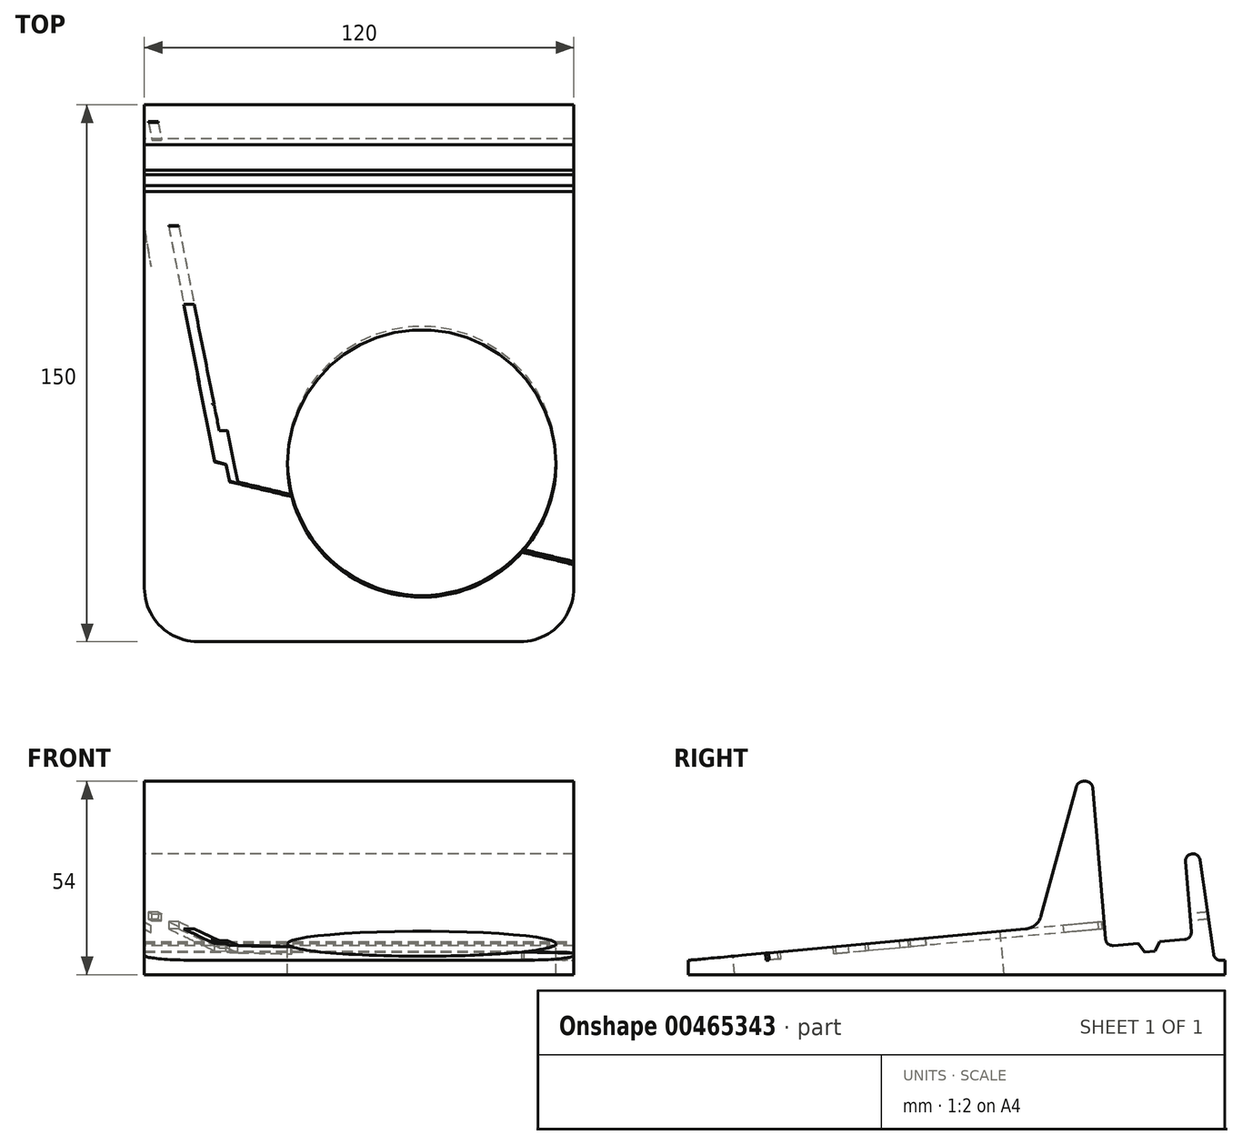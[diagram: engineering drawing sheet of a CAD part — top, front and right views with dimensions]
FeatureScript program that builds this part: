
annotation { "Feature Type Name" : "Feature", "Feature Type Description" : "" }
export const myFeature = defineFeature(function(context is Context, id is Id, definition is map)
    precondition{}
    {
        {
            var Q0;
            Q0=qCreatedBy(makeId("Right.planeOp"),FACE);
            var sketch = newSketch(context, id + "F0", { "sketchPlane" : qUnion([Q0])});
            skLineSegment(sketch, "E0", {"start": v(0, 0) * mm, "end": v(0, 4) * mm});
            skLineSegment(sketch, "E1", {"start": v(150, 4) * mm, "end": v(150, 0) * mm});
            skLineSegment(sketch, "E2", {"start": v(150, 0) * mm, "end": v(0, 0) * mm});
            skLineSegment(sketch, "E3", {"start": v(150, 4) * mm, "end": v(148.73, 4) * mm});
            skLineSegment(sketch, "E4", {"start": v(146.75, 5.71) * mm, "end": v(142.68, 34) * mm});
            skLineSegment(sketch, "E5", {"start": v(142.68, 34) * mm, "end": v(138.72, 33.43) * mm});
            skLineSegment(sketch, "E6", {"start": v(138.72, 33.43) * mm, "end": v(140.53, 12) * mm});
            skPoint(sketch, "E6.endSnap0", {"position": v(140.7, 33.71) * mm});
            skLineSegment(sketch, "E7", {"start": v(138.7, 9.83) * mm, "end": v(118.7, 8.14) * mm});
            skLineSegment(sketch, "E8", {"start": v(116.54, 9.97) * mm, "end": v(112.82, 54) * mm});
            skLineSegment(sketch, "E9", {"start": v(112.82, 54) * mm, "end": v(108.82, 54) * mm});
            skLineSegment(sketch, "E10", {"start": v(108.82, 54) * mm, "end": v(98.58, 16.42) * mm});
            skLineSegment(sketch, "E11", {"start": v(94.22, 12.76) * mm, "end": v(0, 4) * mm});
            skPoint(sketch, "E12.visualSharp", {"position": v(147, 4) * mm});
            skArc(sketch, "E12.filletArc", {"start": v(146.75, 5.71) * mm, "mid": v(147.42, 4.49) * mm, "end": v(148.73, 4) * mm});
            skPoint(sketch, "E13.visualSharp", {"position": v(97.67, 13.08) * mm});
            skArc(sketch, "E13.filletArc", {"start": v(94.22, 12.76) * mm, "mid": v(96.97, 13.91) * mm, "end": v(98.58, 16.42) * mm});
            skPoint(sketch, "E14.visualSharp", {"position": v(116.71, 7.97) * mm});
            skArc(sketch, "E14.filletArc", {"start": v(116.54, 9.97) * mm, "mid": v(117.25, 8.6) * mm, "end": v(118.7, 8.14) * mm});
            skPoint(sketch, "E15.visualSharp", {"position": v(140.7, 10) * mm});
            skArc(sketch, "E15.filletArc", {"start": v(138.7, 9.83) * mm, "mid": v(140.06, 10.53) * mm, "end": v(140.53, 12) * mm});
            skSolve(sketch);
        }
        {
            var Q0;
            Q0=qSketchRegion(id+"F0",true);
            extrude(context, id + "F1", {"entities" : qUnion([Q0]), "offsetDistance" : 25 * mm, "depth" : 120 * mm});
        }
        {
            var Q0;
            Q0=makeQuery(id+"F1.opExtrude","CAP_EDGE",EDGE,{"disambiguationData":[OSD([sQuery(id+"F0.wireOp",EDGE,"E0")])],"isStart":false});
            var Q1;
            Q1=makeQuery(id+"F1.opExtrude","CAP_EDGE",EDGE,{"disambiguationData":[OSD([sQuery(id+"F0.wireOp",EDGE,"E0")])],"isStart":true});
            fillet(context, id + "F2", {"entities" : qUnion([Q0, Q1]), "radius" : 15 * mm, "tangentPropagation" : true, "allowEdgeOverflow" : false});
        }
        {
            var Q0;
            Q0=makeQuery(id+"F1.opExtrude","SWEPT_EDGE",EDGE,{"disambiguationData":[OSD([sQuery(id+"F0.wireOp",EDGE,"E9"),sQuery(id+"F0.wireOp",EDGE,"E10")])]});
            var Q1;
            Q1=makeQuery(id+"F1.opExtrude","SWEPT_EDGE",EDGE,{"disambiguationData":[OSD([sQuery(id+"F0.wireOp",EDGE,"E8"),sQuery(id+"F0.wireOp",EDGE,"E9")])]});
            var Q2;
            Q2=makeQuery(id+"F1.opExtrude","SWEPT_EDGE",EDGE,{"disambiguationData":[OSD([sQuery(id+"F0.wireOp",EDGE,"E5"),sQuery(id+"F0.wireOp",EDGE,"E6")])]});
            var Q3;
            Q3=makeQuery(id+"F1.opExtrude","SWEPT_EDGE",EDGE,{"disambiguationData":[OSD([sQuery(id+"F0.wireOp",EDGE,"E4"),sQuery(id+"F0.wireOp",EDGE,"E5")])]});
            fillet(context, id + "F3", {"entities" : qUnion([Q0, Q1, Q2, Q3]), "radius" : 2 * mm, "tangentPropagation" : true, "allowEdgeOverflow" : false});
        }
        {
            var Q0;
            Q0=makeQuery(id+"F1.opExtrude","SWEPT_BODY",BODY,{"disambiguationData":[OSD([sQuery(id+"F0.wireOp",EDGE,"E0"),sQuery(id+"F0.wireOp",EDGE,"E1"),sQuery(id+"F0.wireOp",EDGE,"E2"),sQuery(id+"F0.wireOp",EDGE,"E3"),sQuery(id+"F0.wireOp",EDGE,"E4"),sQuery(id+"F0.wireOp",EDGE,"E5"),sQuery(id+"F0.wireOp",EDGE,"E6"),sQuery(id+"F0.wireOp",EDGE,"E7"),sQuery(id+"F0.wireOp",EDGE,"E8"),sQuery(id+"F0.wireOp",EDGE,"E9"),sQuery(id+"F0.wireOp",EDGE,"E10"),sQuery(id+"F0.wireOp",EDGE,"E11"),sQuery(id+"F0.wireOp",EDGE,"E12.filletArc"),sQuery(id+"F0.wireOp",EDGE,"E13.filletArc"),sQuery(id+"F0.wireOp",EDGE,"E14.filletArc"),sQuery(id+"F0.wireOp",EDGE,"E15.filletArc")])]});
            transform(context, id + "F4", {"entities" : qUnion([Q0]), "transformType" : TransformType.TRANSLATION_3D, "dx" : 0 * mm, "dy" : 0 * mm, "dz" : 0 * mm, "makeCopy" : true});
        }
        {
            var Q0;
            Q0=makeQuery(id+"F4.opPattern","COPY",FACE,{"derivedFrom":makeQuery(id+"F1.opExtrude","SWEPT_FACE",FACE,{"disambiguationData":[OSD([sQuery(id+"F0.wireOp",EDGE,"E11")])]}),"instanceName":"1"});
            var sketch = newSketch(context, id + "F5", { "sketchPlane" : qUnion([Q0])});
            skCircle(sketch, "E16", {"center": v(77.5, 50.37) * mm, "radius": 37.5 * mm});
            skSolve(sketch);
        }
        {
            var Q0;
            Q0=qSketchRegion(id+"F5",true);
            extrude(context, id + "F6", {"entities" : qUnion([Q0]), "operationType" : NewBodyOperationType.REMOVE, "oppositeDirection" : true, "depth" : 25 * mm});
        }
        {
            var Q0;
            Q0=makeQuery(id+"F1.opExtrude","SWEPT_BODY",BODY,{"disambiguationData":[OSD([sQuery(id+"F0.wireOp",EDGE,"E0"),sQuery(id+"F0.wireOp",EDGE,"E1"),sQuery(id+"F0.wireOp",EDGE,"E2"),sQuery(id+"F0.wireOp",EDGE,"E3"),sQuery(id+"F0.wireOp",EDGE,"E4"),sQuery(id+"F0.wireOp",EDGE,"E5"),sQuery(id+"F0.wireOp",EDGE,"E6"),sQuery(id+"F0.wireOp",EDGE,"E7"),sQuery(id+"F0.wireOp",EDGE,"E8"),sQuery(id+"F0.wireOp",EDGE,"E9"),sQuery(id+"F0.wireOp",EDGE,"E10"),sQuery(id+"F0.wireOp",EDGE,"E11"),sQuery(id+"F0.wireOp",EDGE,"E12.filletArc"),sQuery(id+"F0.wireOp",EDGE,"E13.filletArc"),sQuery(id+"F0.wireOp",EDGE,"E14.filletArc"),sQuery(id+"F0.wireOp",EDGE,"E15.filletArc")])]});
            transform(context, id + "F7", {"entities" : qUnion([Q0]), "transformType" : TransformType.TRANSLATION_3D, "dx" : 0 * mm, "dy" : 0 * mm, "dz" : 0 * mm, "makeCopy" : true});
        }
        {
            var Q0;
            Q0=makeQuery(id+"F1.opExtrude","SWEPT_BODY",BODY,{"disambiguationData":[OSD([sQuery(id+"F0.wireOp",EDGE,"E0"),sQuery(id+"F0.wireOp",EDGE,"E1"),sQuery(id+"F0.wireOp",EDGE,"E2"),sQuery(id+"F0.wireOp",EDGE,"E3"),sQuery(id+"F0.wireOp",EDGE,"E4"),sQuery(id+"F0.wireOp",EDGE,"E5"),sQuery(id+"F0.wireOp",EDGE,"E6"),sQuery(id+"F0.wireOp",EDGE,"E7"),sQuery(id+"F0.wireOp",EDGE,"E8"),sQuery(id+"F0.wireOp",EDGE,"E9"),sQuery(id+"F0.wireOp",EDGE,"E10"),sQuery(id+"F0.wireOp",EDGE,"E11"),sQuery(id+"F0.wireOp",EDGE,"E12.filletArc"),sQuery(id+"F0.wireOp",EDGE,"E13.filletArc"),sQuery(id+"F0.wireOp",EDGE,"E14.filletArc"),sQuery(id+"F0.wireOp",EDGE,"E15.filletArc")])]});
            deleteBodies(context, id + "F8", {"entities" : qUnion([Q0])});
        }
        {
            var Q0;
            Q0=makeQuery(id+"F4.opPattern","COPY",BODY,{"derivedFrom":makeQuery(id+"F1.opExtrude","SWEPT_BODY",BODY,{"disambiguationData":[OSD([sQuery(id+"F0.wireOp",EDGE,"E0"),sQuery(id+"F0.wireOp",EDGE,"E1"),sQuery(id+"F0.wireOp",EDGE,"E2"),sQuery(id+"F0.wireOp",EDGE,"E3"),sQuery(id+"F0.wireOp",EDGE,"E4"),sQuery(id+"F0.wireOp",EDGE,"E5"),sQuery(id+"F0.wireOp",EDGE,"E6"),sQuery(id+"F0.wireOp",EDGE,"E7"),sQuery(id+"F0.wireOp",EDGE,"E8"),sQuery(id+"F0.wireOp",EDGE,"E9"),sQuery(id+"F0.wireOp",EDGE,"E10"),sQuery(id+"F0.wireOp",EDGE,"E11"),sQuery(id+"F0.wireOp",EDGE,"E12.filletArc"),sQuery(id+"F0.wireOp",EDGE,"E13.filletArc"),sQuery(id+"F0.wireOp",EDGE,"E14.filletArc"),sQuery(id+"F0.wireOp",EDGE,"E15.filletArc")])]}),"instanceName":"1"});
            deleteBodies(context, id + "F9", {"entities" : qUnion([Q0])});
        }
        {
            var Q0;
            Q0=makeQuery(id+"F7.opPattern","COPY",FACE,{"derivedFrom":makeQuery(id+"F1.opExtrude","SWEPT_FACE",FACE,{"disambiguationData":[OSD([sQuery(id+"F0.wireOp",EDGE,"E11")])]}),"instanceName":"1"});
            var sketch = newSketch(context, id + "F10", { "sketchPlane" : qUnion([Q0])});
            skLineSegment(sketch, "E17", {"start": v(11.27, 59.35) * mm, "end": v(12.93, 59.25) * mm});
            skLineSegment(sketch, "E18", {"start": v(12.93, 59.25) * mm, "end": v(12.93, 52.54) * mm});
            skLineSegment(sketch, "E19", {"start": v(20.34, 67.04) * mm, "end": v(18.96, 67.04) * mm});
            skLineSegment(sketch, "E20", {"start": v(20.34, 62.07) * mm, "end": v(20.34, 64.54) * mm});
            skLineSegment(sketch, "E21", {"start": v(20.34, 64.54) * mm, "end": v(20.34, 67.04) * mm});
            skLineSegment(sketch, "E22", {"start": v(48.14, 58.86) * mm, "end": v(49.44, 58.75) * mm});
            skLineSegment(sketch, "E23", {"start": v(55.97, 56.74) * mm, "end": v(57.27, 57.87) * mm});
            skLineSegment(sketch, "E24", {"start": v(55.97, 50.67) * mm, "end": v(55.97, 56.74) * mm});
            skLineSegment(sketch, "E25", {"start": v(49.44, 58.75) * mm, "end": v(49.44, 52.05) * mm});
            skLineSegment(sketch, "E26", {"start": v(64.44, 56.14) * mm, "end": v(64.44, 50.74) * mm});
            skLineSegment(sketch, "E27", {"start": v(26.69, 60.97) * mm, "end": v(26.69, 62.28) * mm});
            skLineSegment(sketch, "E28", {"start": v(20.34, 53.81) * mm, "end": v(20.34, 59.63) * mm});
            skLineSegment(sketch, "E29", {"start": v(63.2, 57.41) * mm, "end": v(64.44, 56.14) * mm});
            skLineSegment(sketch, "E30", {"start": v(26.69, 59.63) * mm, "end": v(26.69, 60.97) * mm});
            skLineSegment(sketch, "E31", {"start": v(20.34, 59.63) * mm, "end": v(23.51, 59.63) * mm});
            skLineSegment(sketch, "E32", {"start": v(23.51, 59.63) * mm, "end": v(26.69, 59.63) * mm});
            skLineSegment(sketch, "E33", {"start": v(23.51, 62.17) * mm, "end": v(20.34, 62.07) * mm});
            skLineSegment(sketch, "E34", {"start": v(33.28, 58.22) * mm, "end": v(34.55, 59.46) * mm});
            skLineSegment(sketch, "E35", {"start": v(34.06, 57.38) * mm, "end": v(33.28, 58.22) * mm});
            skLineSegment(sketch, "E36", {"start": v(26.69, 62.28) * mm, "end": v(23.51, 62.17) * mm});
            skFitSpline(sketch, "E37", {"points": [v(13.6, 44.5) * mm, v(1000, 14.87) * mm, v(42.07, 1000) * mm, v(18.82, 41) * mm]});
            skFitSpline(sketch, "E38", {"points": [v(26.34, 45) * mm, v(1000, 26.34) * mm, v(45.77, 1000) * mm, v(26.26, 45.8) * mm]});
            skFitSpline(sketch, "E39", {"points": [v(9.47, 60.23) * mm, v(1000, 9.58) * mm, v(59.56, 1000) * mm, v(9.83, 59.46) * mm]});
            skFitSpline(sketch, "E40", {"points": [v(22.56, 42.14) * mm, v(1000, 24.82) * mm, v(42.8, 1000) * mm, v(26.34, 43.97) * mm]});
            skFitSpline(sketch, "E41", {"points": [v(25.24, 45.45) * mm, v(1000, 24.47) * mm, v(45.17, 1000) * mm, v(23.8, 45.2) * mm]});
            skFitSpline(sketch, "E42", {"points": [v(12.93, 52.54) * mm, v(1000, 12.93) * mm, v(46.62, 1000) * mm, v(13, 45.7) * mm]});
            skFitSpline(sketch, "E43", {"points": [v(22.77, 45.49) * mm, v(1000, 20.59) * mm, v(46.16, 1000) * mm, v(20.34, 46.97) * mm]});
            skFitSpline(sketch, "E44", {"points": [v(47.89, 61.05) * mm, v(1000, 46.9) * mm, v(61.05, 1000) * mm, v(46.8, 60.94) * mm]});
            skFitSpline(sketch, "E45", {"points": [v(46.8, 60.02) * mm, v(1000, 46.8) * mm, v(59.07, 1000) * mm, v(46.9, 58.96) * mm]});
            skFitSpline(sketch, "E46", {"points": [v(12.5, 62.5) * mm, v(1000, 9.8) * mm, v(61.22, 1000) * mm, v(9.37, 60.94) * mm]});
            skFitSpline(sketch, "E47", {"points": [v(60.27, 58.86) * mm, v(1000, 61.65) * mm, v(58.72, 1000) * mm, v(62.21, 58.43) * mm]});
            skFitSpline(sketch, "E48", {"points": [v(52.97, 62.53) * mm, v(1000, 51.63) * mm, v(61.72, 1000) * mm, v(49.3, 61.05) * mm]});
            skFitSpline(sketch, "E49", {"points": [v(18.96, 67.04) * mm, v(1000, 17.76) * mm, v(67.04, 1000) * mm, v(17.52, 66.9) * mm]});
            skFitSpline(sketch, "E50", {"points": [v(57.27, 57.87) * mm, v(1000, 58.44) * mm, v(58.9, 1000) * mm, v(58.72, 59) * mm]});
            skFitSpline(sketch, "E51", {"points": [v(58.5, 42.49) * mm, v(1000, 56.18) * mm, v(43.3, 1000) * mm, v(55.97, 43.94) * mm]});
            skFitSpline(sketch, "E52", {"points": [v(52.86, 42.03) * mm, v(1000, 58.61) * mm, v(42.03, 1000) * mm, v(59.5, 42.1) * mm]});
            skFitSpline(sketch, "E53", {"points": [v(47.43, 42.8) * mm, v(1000, 44.75) * mm, v(42.28, 1000) * mm, v(46.66, 42) * mm]});
            skFitSpline(sketch, "E54", {"points": [v(49.44, 52.05) * mm, v(1000, 49.44) * mm, v(44.43, 1000) * mm, v(49.16, 43.16) * mm]});
            skFitSpline(sketch, "E55", {"points": [v(31.3, 47.08) * mm, v(1000, 30.46) * mm, v(47.96, 1000) * mm, v(29.76, 48.35) * mm]});
            skFitSpline(sketch, "E56", {"points": [v(36.78, 44.46) * mm, v(1000, 34.8) * mm, v(44.46, 1000) * mm, v(32.97, 45.35) * mm]});
            skFitSpline(sketch, "E57", {"points": [v(40.98, 46.12) * mm, v(1000, 40.62) * mm, v(45.28, 1000) * mm, v(38.58, 44.46) * mm]});
            skFitSpline(sketch, "E58", {"points": [v(37.9, 49.26) * mm, v(1000, 39.85) * mm, v(48.3, 1000) * mm, v(41.26, 46.86) * mm]});
            skFitSpline(sketch, "E59", {"points": [v(34.27, 62.35) * mm, v(1000, 30.53) * mm, v(61.47, 1000) * mm, v(28.45, 59.46) * mm]});
            skFitSpline(sketch, "E60", {"points": [v(33.28, 51.56) * mm, v(1000, 34.98) * mm, v(50.7, 1000) * mm, v(37.06, 49.69) * mm]});
            skFitSpline(sketch, "E61", {"points": [v(28.45, 56.81) * mm, v(1000, 28.45) * mm, v(54.55, 1000) * mm, v(29.55, 53.35) * mm]});
            skFitSpline(sketch, "E62", {"points": [v(55.02, 63.16) * mm, v(1000, 54.45) * mm, v(63.16, 1000) * mm, v(53.57, 62.88) * mm]});
            skFitSpline(sketch, "E63", {"points": [v(55.97, 61.57) * mm, v(1000, 55.97) * mm, v(63.06, 1000) * mm, v(55.9, 63.16) * mm]});
            skFitSpline(sketch, "E64", {"points": [v(59.5, 61.05) * mm, v(1000, 56.07) * mm, v(59.63, 1000) * mm, v(55.97, 59.67) * mm]});
            skFitSpline(sketch, "E65", {"points": [v(64.68, 62.1) * mm, v(1000, 62.57) * mm, v(62.1, 1000) * mm, v(61.54, 61.9) * mm]});
            skFitSpline(sketch, "E66", {"points": [v(69.97, 60.23) * mm, v(1000, 68.2) * mm, v(61.79, 1000) * mm, v(67.33, 62.1) * mm]});
            skFitSpline(sketch, "E67", {"points": [v(29.09, 48.35) * mm, v(1000, 28) * mm, v(48.35, 1000) * mm, v(27.96, 48.17) * mm]});
            skFitSpline(sketch, "E68", {"points": [v(28.95, 43.44) * mm, v(1000, 29.05) * mm, v(42.67, 1000) * mm, v(29.26, 42.56) * mm]});
            skFitSpline(sketch, "E69", {"points": [v(44.19, 43.23) * mm, v(1000, 44.47) * mm, v(43.51, 1000) * mm, v(44.9, 43.86) * mm]});
            skFitSpline(sketch, "E70", {"points": [v(42.14, 42.45) * mm, v(1000, 42.99) * mm, v(42.6, 1000) * mm, v(43.9, 42.95) * mm]});
            skFitSpline(sketch, "E71", {"points": [v(31.13, 42.38) * mm, v(1000, 34.17) * mm, v(42.14, 1000) * mm, v(40.38, 42.14) * mm]});
            skFitSpline(sketch, "E72", {"points": [v(28.49, 45.88) * mm, v(1000, 28.7) * mm, v(45, 1000) * mm, v(28.91, 43.9) * mm]});
            skFitSpline(sketch, "E73", {"points": [v(70.43, 50.85) * mm, v(1000, 70.43) * mm, v(56.64, 1000) * mm, v(70.71, 57.48) * mm]});
            skFitSpline(sketch, "E74", {"points": [v(16.63, 65.5) * mm, v(1000, 15.79) * mm, v(64.15, 1000) * mm, v(15.19, 63.7) * mm]});
            skFitSpline(sketch, "E75", {"points": [v(77.38, 42.56) * mm, v(1000, 76.36) * mm, v(42.1, 1000) * mm, v(76.82, 42.07) * mm]});
            skFitSpline(sketch, "E76", {"points": [v(62.42, 42.77) * mm, v(1000, 61.97) * mm, v(42.7, 1000) * mm, v(61.61, 42.49) * mm]});
            skFitSpline(sketch, "E77", {"points": [v(72.7, 42.52) * mm, v(1000, 70.9) * mm, v(43.34, 1000) * mm, v(70.43, 45.03) * mm]});
            skFitSpline(sketch, "E78", {"points": [v(64.44, 50.74) * mm, v(1000, 64.44) * mm, v(44.78, 1000) * mm, v(63.98, 42.98) * mm]});
            skFitSpline(sketch, "E79", {"points": [v(87.3, 42.52) * mm, v(1000, 85.92) * mm, v(43.3, 1000) * mm, v(85.6, 44.89) * mm]});
            skFitSpline(sketch, "E80", {"points": [v(67.72, 42.03) * mm, v(1000, 73.15) * mm, v(42.07, 1000) * mm, v(73.68, 42.1) * mm]});
            skFitSpline(sketch, "E81", {"points": [v(72.9, 58.36) * mm, v(1000, 74.74) * mm, v(59.1, 1000) * mm, v(76, 59.07) * mm]});
            skFitSpline(sketch, "E82", {"points": [v(77.24, 58.3) * mm, v(1000, 79.15) * mm, v(57.02, 1000) * mm, v(79.22, 56.7) * mm]});
            skFitSpline(sketch, "E83", {"points": [v(61.61, 42.31) * mm, v(1000, 61.61) * mm, v(42.14, 1000) * mm, v(64.15, 42) * mm]});
            skFitSpline(sketch, "E84", {"points": [v(85.6, 51.52) * mm, v(1000, 85.57) * mm, v(58.26, 1000) * mm, v(85.14, 59.95) * mm]});
            skFitSpline(sketch, "E85", {"points": [v(83.17, 61.3) * mm, v(1000, 82.18) * mm, v(61.96, 1000) * mm, v(81.47, 62.1) * mm]});
            skFitSpline(sketch, "E86", {"points": [v(79.43, 62.1) * mm, v(1000, 77.28) * mm, v(62.1, 1000) * mm, v(76.36, 61.9) * mm]});
            skFitSpline(sketch, "E87", {"points": [v(73.78, 60.83) * mm, v(1000, 70.75) * mm, v(59.56, 1000) * mm, v(70.75, 59.56) * mm]});
            skFitSpline(sketch, "E88", {"points": [v(103.2, 58.43) * mm, v(1000, 104.37) * mm, v(56.74, 1000) * mm, v(106.24, 55.05) * mm]});
            skFitSpline(sketch, "E89", {"points": [v(94.77, 42.35) * mm, v(1000, 97.24) * mm, v(41.57, 1000) * mm, v(101.51, 41.4) * mm]});
            skFitSpline(sketch, "E90", {"points": [v(39.39, 59.32) * mm, v(1000, 39.5) * mm, v(59.18, 1000) * mm, v(40.13, 58.68) * mm]});
            skFitSpline(sketch, "E91", {"points": [v(41.68, 62.24) * mm, v(1000, 40.52) * mm, v(62.32, 1000) * mm, v(38.79, 62.46) * mm]});
            skFitSpline(sketch, "E92", {"points": [v(34.55, 59.46) * mm, v(1000, 35.26) * mm, v(60.16, 1000) * mm, v(36.18, 60.7) * mm]});
            skFitSpline(sketch, "E93", {"points": [v(44.33, 56.28) * mm, v(1000, 45.24) * mm, v(56.5, 1000) * mm, v(45.35, 56.64) * mm]});
            skFitSpline(sketch, "E94", {"points": [v(45.14, 44) * mm, v(1000, 45.95) * mm, v(44.54, 1000) * mm, v(46.8, 46.2) * mm]});
            skFitSpline(sketch, "E95", {"points": [v(42.7, 56.6) * mm, v(1000, 43.1) * mm, v(56.21, 1000) * mm, v(43.59, 56.1) * mm]});
            skFitSpline(sketch, "E96", {"points": [v(98.76, 46.4) * mm, v(1000, 95.06) * mm, v(47.46, 1000) * mm, v(93.36, 49.58) * mm]});
            skFitSpline(sketch, "E97", {"points": [v(107.8, 61.08) * mm, v(1000, 105.4) * mm, v(62.28, 1000) * mm, v(100.1, 62.77) * mm]});
            skFitSpline(sketch, "E98", {"points": [v(110.26, 46.55) * mm, v(1000, 111.7) * mm, v(48.56, 1000) * mm, v(110.68, 49.86) * mm]});
            skFitSpline(sketch, "E99", {"points": [v(37.8, 62.56) * mm, v(1000, 36.85) * mm, v(62.67, 1000) * mm, v(35.26, 62.56) * mm]});
            skFitSpline(sketch, "E100", {"points": [v(108.96, 48.24) * mm, v(1000, 106.3) * mm, v(45.77, 1000) * mm, v(103.06, 45.17) * mm]});
            skFitSpline(sketch, "E101", {"points": [v(103.13, 42.03) * mm, v(1000, 103.66) * mm, v(42.24, 1000) * mm, v(104.4, 42.45) * mm]});
            skFitSpline(sketch, "E102", {"points": [v(87.82, 48.45) * mm, v(1000, 88.39) * mm, v(46.2, 1000) * mm, v(91.63, 43.37) * mm]});
            skFitSpline(sketch, "E103", {"points": [v(44.43, 51.73) * mm, v(1000, 43.06) * mm, v(52.75, 1000) * mm, v(39.5, 54.7) * mm]});
            skFitSpline(sketch, "E104", {"points": [v(39.04, 54.7) * mm, v(1000, 38.3) * mm, v(54.7, 1000) * mm, v(34.84, 56.56) * mm]});
            skFitSpline(sketch, "E105", {"points": [v(43.87, 62.03) * mm, v(1000, 43.83) * mm, v(62.1, 1000) * mm, v(42.85, 62.2) * mm]});
            skFitSpline(sketch, "E106", {"points": [v(96.6, 62.07) * mm, v(1000, 89.87) * mm, v(60.76, 1000) * mm, v(86.24, 55.12) * mm]});
            skFitSpline(sketch, "E107", {"points": [v(45.17, 57.45) * mm, v(1000, 44.9) * mm, v(58.61, 1000) * mm, v(43.97, 61.9) * mm]});
            skFitSpline(sketch, "E108", {"points": [v(104.72, 42.52) * mm, v(1000, 105.75) * mm, v(42.74, 1000) * mm, v(109.48, 45.45) * mm]});
            skFitSpline(sketch, "E109", {"points": [v(46.8, 47.29) * mm, v(1000, 46.8) * mm, v(48.73, 1000) * mm, v(45.7, 50.81) * mm]});
            skFitSpline(sketch, "E110", {"points": [v(98.94, 59.99) * mm, v(1000, 100.95) * mm, v(60.62, 1000) * mm, v(101.97, 60.23) * mm]});
            skFitSpline(sketch, "E111", {"points": [v(93.36, 53.21) * mm, v(1000, 93.36) * mm, v(56.42, 1000) * mm, v(95.44, 58.96) * mm]});
            skFitSpline(sketch, "E112", {"points": [v(106.87, 55.05) * mm, v(1000, 107.83) * mm, v(55.05, 1000) * mm, v(109.94, 55.82) * mm]});
            skFitSpline(sketch, "E113", {"points": [v(40.87, 58.15) * mm, v(1000, 41.58) * mm, v(57.62, 1000) * mm, v(42.39, 56.92) * mm]});
            skFitSpline(sketch, "E114", {"points": [v(36.64, 60.7) * mm, v(1000, 37.34) * mm, v(60.7, 1000) * mm, v(38.82, 59.95) * mm]});
            skFitSpline(sketch, "E115", {"points": [v(110.47, 56.35) * mm, v(1000, 111.6) * mm, v(57.48, 1000) * mm, v(110.3, 59.78) * mm]});
            skFitSpline(sketch, "E116", {"points": [v(82.25, 42.03) * mm, v(1000, 87.72) * mm, v(42.03, 1000) * mm, v(88.18, 42.07) * mm]});
            skFitSpline(sketch, "E117", {"points": [v(79.25, 51) * mm, v(1000, 79.25) * mm, v(44.6, 1000) * mm, v(78.93, 43.23) * mm]});
            skSolve(sketch);
        }
        {
            var Q0;
            Q0 = qSketchRegion(id + "F10", true);
            var Q1;
            Q1=makeQuery(id+"F10.imprint","IMPRINT",FACE,{"disambiguationData":[TD([[makeQuery(id+"F10.imprint","IMPRINT",EDGE,{"derivedFrom":sQuery(id+"F10.wireOp",EDGE,"RX8xWYy4-PQok-bXDF-rX3b-FTFGcYQA8Ppw")}),1.0]])]});
            extrude(context, id + "F11", {"entities" : qUnion([Q0, Q1]), "operationType" : NewBodyOperationType.REMOVE, "oppositeDirection" : true, "depth" : 2 * mm});
        }
        {
            var Q0;
            Q0=makeQuery(id+"F7.opPattern","COPY",FACE,{"derivedFrom":makeQuery(id+"F1.opExtrude","CAP_FACE",FACE,{"disambiguationData":[OSD([sQuery(id+"F0.wireOp",EDGE,"E0"),sQuery(id+"F0.wireOp",EDGE,"E1"),sQuery(id+"F0.wireOp",EDGE,"E2"),sQuery(id+"F0.wireOp",EDGE,"E3"),sQuery(id+"F0.wireOp",EDGE,"E4"),sQuery(id+"F0.wireOp",EDGE,"E5"),sQuery(id+"F0.wireOp",EDGE,"E6"),sQuery(id+"F0.wireOp",EDGE,"E7"),sQuery(id+"F0.wireOp",EDGE,"E8"),sQuery(id+"F0.wireOp",EDGE,"E9"),sQuery(id+"F0.wireOp",EDGE,"E10"),sQuery(id+"F0.wireOp",EDGE,"E11"),sQuery(id+"F0.wireOp",EDGE,"E12.filletArc"),sQuery(id+"F0.wireOp",EDGE,"E13.filletArc"),sQuery(id+"F0.wireOp",EDGE,"E14.filletArc"),sQuery(id+"F0.wireOp",EDGE,"E15.filletArc")])],"isStart":false}),"instanceName":"1"});
            var sketch = newSketch(context, id + "F12", { "sketchPlane" : qUnion([Q0])});
            skLineSegment(sketch, "E118", {"start": v(128.7, 8.99) * mm, "end": v(129.17, 3.48) * mm});
            skCircle(sketch, "E119.cCircle", {"center": v(128.7, 8.99) * mm, "radius": 2.6 * mm, "construction": true});
            skLineSegment(sketch, "E119.0", {"start": v(130.42, 6.52) * mm, "end": v(127.43, 6.27) * mm});
            skLineSegment(sketch, "E119.1", {"start": v(127.43, 6.27) * mm, "end": v(125.72, 8.73) * mm});
            skLineSegment(sketch, "E119.2", {"start": v(125.72, 8.73) * mm, "end": v(127, 11.45) * mm});
            skLineSegment(sketch, "E119.3", {"start": v(127, 11.45) * mm, "end": v(129.98, 11.7) * mm});
            skLineSegment(sketch, "E119.4", {"start": v(129.98, 11.7) * mm, "end": v(131.7, 9.24) * mm});
            skLineSegment(sketch, "E119.5", {"start": v(131.7, 9.24) * mm, "end": v(130.42, 6.52) * mm});
            skPoint(sketch, "E119.0.midPoint", {"position": v(128.92, 6.4) * mm});
            skSolve(sketch);
        }
        {
            var Q0;
            {var subQ5=sQuery(id+"F12.wireOp",EDGE,"E119.1");Q0=makeQuery(id+"F12.imprint","IMPRINT",FACE,{"disambiguationData":[TD([[makeQuery(id+"F12.imprint","IMPRINT",EDGE,{"derivedFrom":subQ5}),-1.0]])]});}
            var Q1;
            {var subQ5=sQuery(id+"F12.wireOp",EDGE,"E119.5");Q1=makeQuery(id+"F12.imprint","IMPRINT",FACE,{"disambiguationData":[TD([[makeQuery(id+"F12.imprint","IMPRINT",EDGE,{"derivedFrom":subQ5}),-1.0]])]});}
            extrude(context, id + "F13", {"entities" : qUnion([Q0, Q1]), "operationType" : NewBodyOperationType.REMOVE, "oppositeDirection" : true, "depth" : 120 * mm, "offsetDistance" : 25 * mm});
        }
    });
